# Revit family: Medical_OR-Table
name_source: partatom
category: Specialty Equipment
units: mm (PartAtom-declared; Revit-internal decimal feet)

## family parameters
Always vertical = Yes
Classification Number = 23.40.70.14.21
Cut with Voids When Loaded = No
Enable Cutting in Views = No
Maintain Annotation Orientation = No
Part Type = Normal
Room Calculation Point = No
Round Connector Dimension = Use Diameter
Shared = No
Work Plane-Based = No

## types (1)
- ByType
    Assembly Code = E1020810
    Base Material = ARCAT - Plastic - ABS - White
    Capacity_Lbs = 300
    Casters = ARCAT - Plastic - ABS - Black
    Construction Details = http://www.arcat.com
    Control Mechanics = ARCAT - Metal - Brass - BHMA609 - Dull Brass - Oxidized
    Cushion Material = ARCAT - Textiles - Vinyl - Blue
    Default Elevation = 0' - 0"
    Description = Operating Room Table
    Expected Lifespan (Years) = 5
    Green Building-LEED = http://www.arcat.com
    Hardware and Controls = ARCAT - Metal - Steel - BHMA632 - Bright Brass
    Keynote = 11760
    Maintenance Schedule (Months) = 3
    Manufacturer = Generic
    Manufacturer Fax = (203) 939-2444
    Manufacturer Website = http://www.arcat.com
    Model = Generic
    Product Data = http://www.arcat.com
    Product Properties = http://www.arcat.com
    Range - Kindney Elevator = 4.5 Inches
    Range - Raise-Lower = 0-90 Inches
    Range - Reverse Trendelenburg ( Head Up) = 0-20 Inches
    Range - Tilt L-R = 0-10 Inches
    Range - Trendelenburg ( Head Down) = 0-20 Inches
    Specification = http://www.arcat.com
    Table Material = ARCAT - Plastic - HDPE - White
    Warranty Duration (Years) = 1

## geometry (parser evidence)
native form markers: Blend x3, Sweep x4
no freeform markers — native parametric forms only
